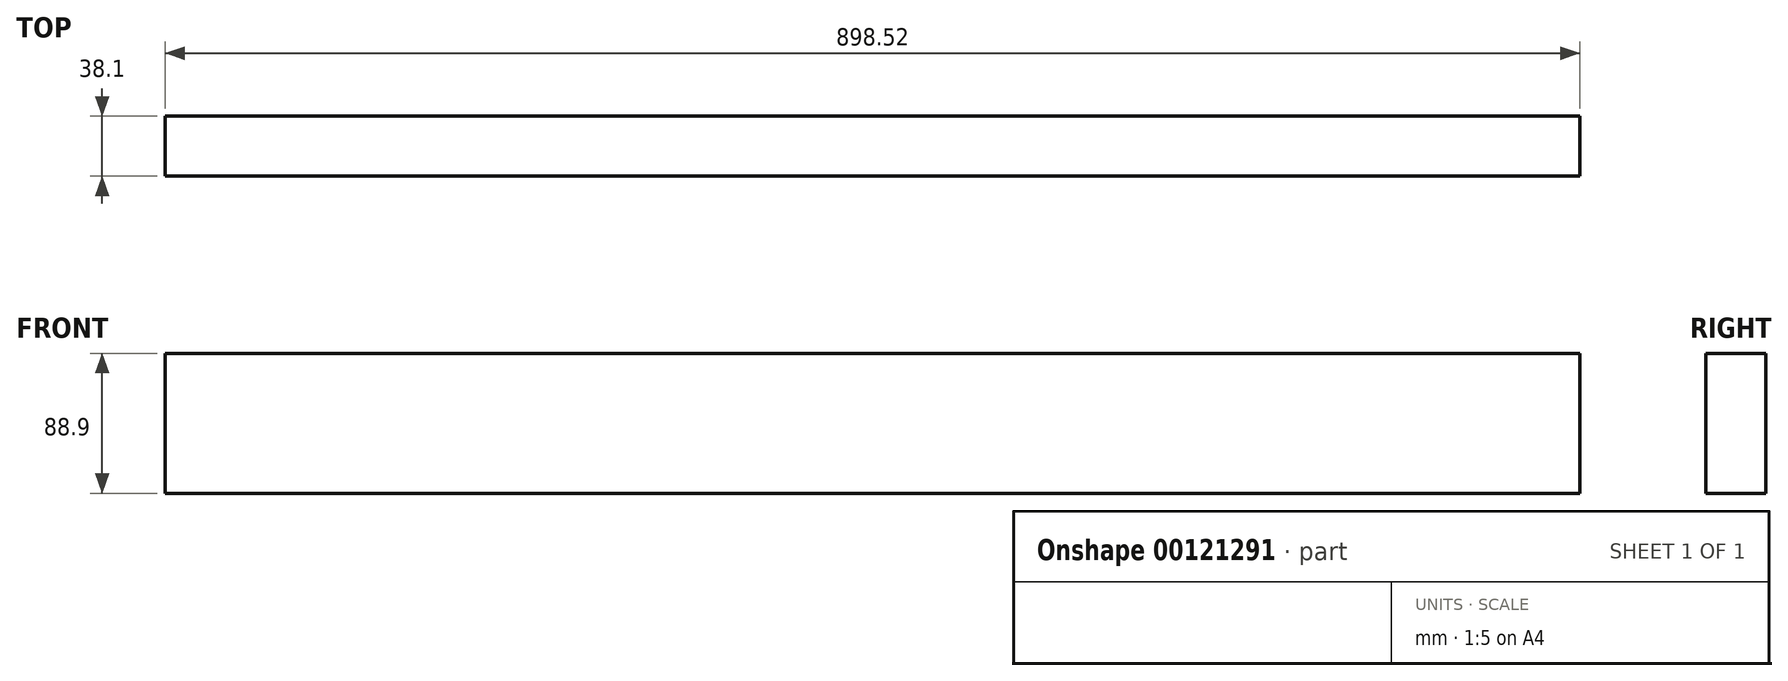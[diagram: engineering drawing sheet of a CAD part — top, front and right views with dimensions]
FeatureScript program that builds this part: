
annotation { "Feature Type Name" : "Feature", "Feature Type Description" : "" }
export const myFeature = defineFeature(function(context is Context, id is Id, definition is map)
    precondition{}
    {
        {
            var Q0;
            Q0=qCreatedBy(makeId("Front.planeOp"),FACE);
            var sketch = newSketch(context, id + "F0", { "sketchPlane" : qUnion([Q0])});
            skLineSegment(sketch, "E0.bottom", {"start": v(0, 0) * mm, "end": v(898.52, 0) * mm});
            skLineSegment(sketch, "E0.top", {"start": v(0, 88.9) * mm, "end": v(898.52, 88.9) * mm});
            skLineSegment(sketch, "E0.left", {"start": v(0, 0) * mm, "end": v(0, 88.9) * mm});
            skLineSegment(sketch, "E0.right", {"start": v(898.52, 0) * mm, "end": v(898.52, 88.9) * mm});
            skSolve(sketch);
        }
        {
            var Q0;
            Q0=makeQuery(id+"F0.imprint","IMPRINT",FACE,{"disambiguationData":[TD([[makeQuery(id+"F0.imprint","IMPRINT",EDGE,{"derivedFrom":sQuery(id+"F0.wireOp",EDGE,"E0.bottom")}),1.0]])]});
            extrude(context, id + "F1", {"entities" : qUnion([Q0]), "depth" : 38.1 * mm});
        }
    });
